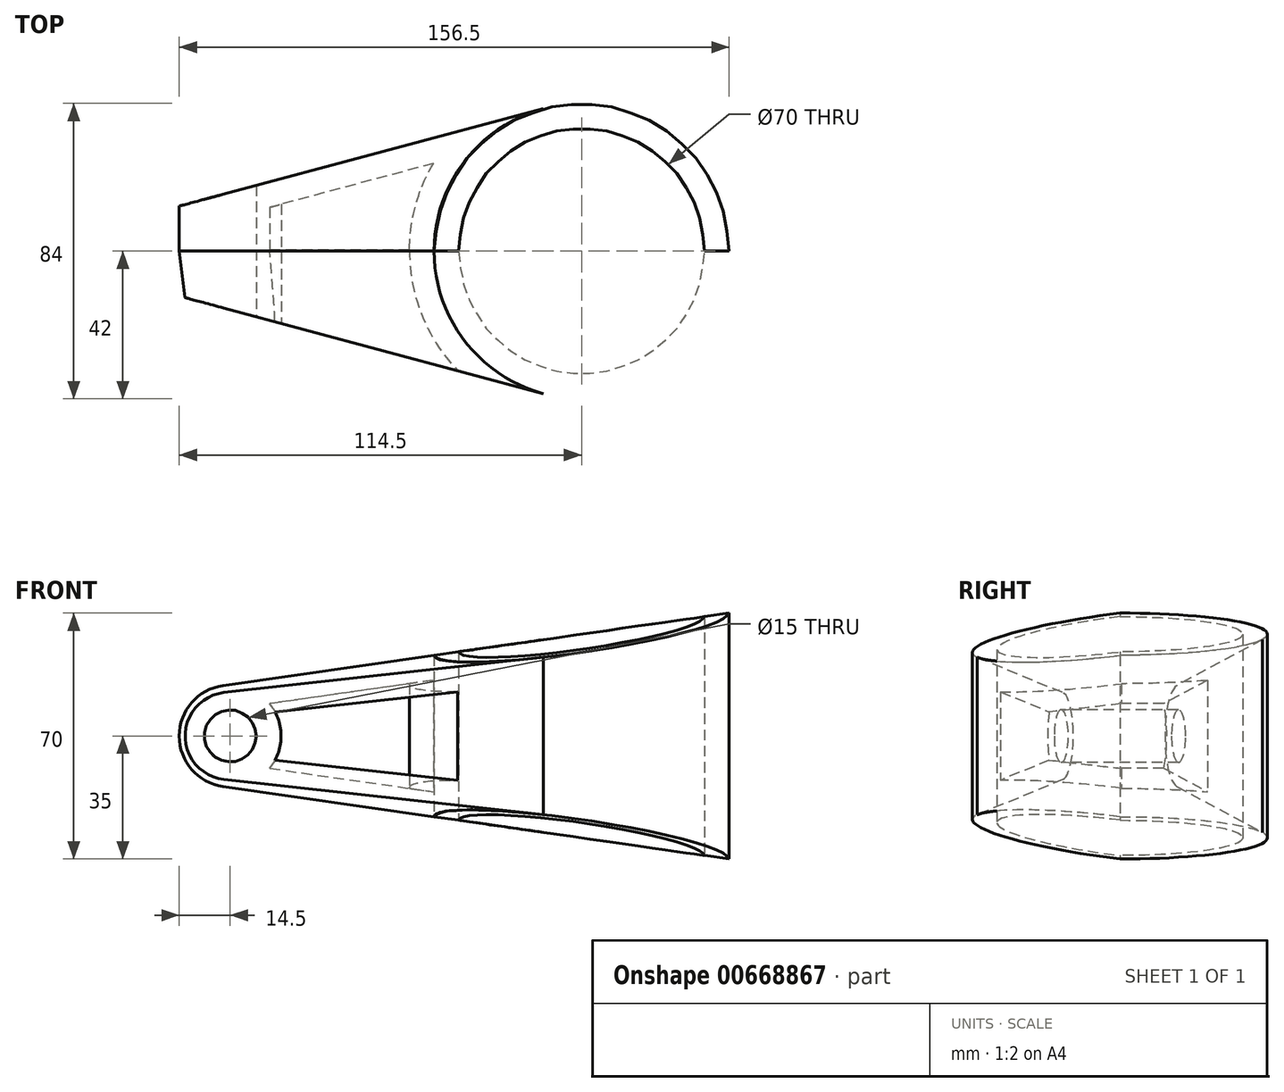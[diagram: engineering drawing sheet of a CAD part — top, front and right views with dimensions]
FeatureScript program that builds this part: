
annotation { "Feature Type Name" : "Feature", "Feature Type Description" : "" }
export const myFeature = defineFeature(function(context is Context, id is Id, definition is map)
    precondition{}
    {
        {
            var Q0;
            Q0=qCreatedBy(makeId("Top.planeOp"),FACE);
            var sketch = newSketch(context, id + "F0", { "sketchPlane" : qUnion([Q0])});
            skCircle(sketch, "E0", {"center": v(0, 0) * mm, "radius": 35 * mm});
            skCircle(sketch, "E1.0", {"center": v(0, 0) * mm, "radius": 42 * mm});
            skLineSegment(sketch, "E2", {"start": v(-100, 39.97) * mm, "end": v(-100, -35.77) * mm, "construction": true});
            skLineSegment(sketch, "E3.0", {"start": v(-114.5, 39.97) * mm, "end": v(-114.5, -35.77) * mm, "construction": true});
            skLineSegment(sketch, "E4", {"start": v(-10.87, 40.57) * mm, "end": v(-114.5, 12.8) * mm});
            skLineSegment(sketch, "E5", {"start": v(-114.5, 12.8) * mm, "end": v(-114.5, -12.8) * mm});
            skLineSegment(sketch, "E6", {"start": v(-114.5, -12.8) * mm, "end": v(-10.87, -40.57) * mm});
            skSolve(sketch);
        }
        {
            var Q0;
            Q0=makeQuery(id+"F0.imprint","IMPRINT",FACE,{"disambiguationData":[TD([[makeQuery(id+"F0.imprint","IMPRINT",EDGE,{"derivedFrom":sQuery(id+"F0.wireOp",EDGE,"E0")}),-1.0]])]});
            extrude(context, id + "F1", {"entities" : qUnion([Q0]), "endBound" : BoundingType.SYMMETRIC, "depth" : 70 * mm, "offsetDistance" : 25 * mm});
        }
        {
            var Q0;
            {var subQ0=sQuery(id+"F0.wireOp",EDGE,"E4");Q0=makeQuery(id+"F0.imprint","IMPRINT",FACE,{"disambiguationData":[TD([[makeQuery(id+"F0.imprint","IMPRINT",EDGE,{"derivedFrom":subQ0}),1.0]])]});}
            extrude(context, id + "F2", {"entities" : qUnion([Q0]), "endBound" : BoundingType.SYMMETRIC, "depth" : 70 * mm, "offsetDistance" : 25 * mm});
        }
        {
            var Q0;
            Q0=qCreatedBy(makeId("Front.planeOp"),FACE);
            var sketch = newSketch(context, id + "F3", { "sketchPlane" : qUnion([Q0])});
            skLineSegment(sketch, "E7.0", {"start": v(-42, 0) * mm, "end": v(42, 0) * mm});
            skCircle(sketch, "E8", {"center": v(-100, 0) * mm, "radius": 7.5 * mm});
            skLineSegment(sketch, "E9", {"start": v(42, 35) * mm, "end": v(-102.06, 14.35) * mm});
            skArc(sketch, "E10", {"start": v(-102.06, 14.35) * mm, "mid": v(-114.5, 0) * mm, "end": v(-102.06, -14.35) * mm});
            skLineSegment(sketch, "E11", {"start": v(-102.06, -14.35) * mm, "end": v(42, -35) * mm});
            skLineSegment(sketch, "E12", {"start": v(42, 35) * mm, "end": v(42, -35) * mm});
            skLineSegment(sketch, "E13", {"start": v(-42, -22.96) * mm, "end": v(-42, 22.96) * mm});
            skLineSegment(sketch, "E14.0", {"start": v(-42, 35) * mm, "end": v(42, 35) * mm});
            skLineSegment(sketch, "E15.0", {"start": v(-42, -35) * mm, "end": v(42, -35) * mm});
            skLineSegment(sketch, "E16.0.0", {"start": v(-10.87, 35) * mm, "end": v(-42, 35) * mm});
            skLineSegment(sketch, "E16.0.1", {"start": v(-10.87, 35) * mm, "end": v(-114.5, 35) * mm});
            skLineSegment(sketch, "E16.0.3", {"start": v(-114.5, 35) * mm, "end": v(-10.87, 35) * mm});
            skLineSegment(sketch, "E17.0.0", {"start": v(-114.5, -35) * mm, "end": v(-10.87, -35) * mm});
            skLineSegment(sketch, "E17.0.1", {"start": v(-10.87, -27.42) * mm, "end": v(-10.87, 27.42) * mm});
            skLineSegment(sketch, "E17.0.3", {"start": v(-114.5, 35) * mm, "end": v(-114.5, -35) * mm});
            skSolve(sketch);
        }
        {
            var Q0;
            {var subQ7=sQuery(id+"F3.wireOp",EDGE,"E14.0");Q0=makeQuery(id+"F3.imprint","IMPRINT",FACE,{"disambiguationData":[TD([[makeQuery(id+"F3.imprint","IMPRINT",EDGE,{"derivedFrom":subQ7}),-1.0]])]});}
            var Q1;
            {var subQ0=sQuery(id+"F3.wireOp",EDGE,"E15.0");Q1=makeQuery(id+"F3.imprint","IMPRINT",FACE,{"disambiguationData":[TD([[makeQuery(id+"F3.imprint","IMPRINT",EDGE,{"derivedFrom":subQ0}),1.0]])]});}
            var Q2;
            Q2=makeQuery(id+"F3.imprint","IMPRINT",FACE,{"disambiguationData":[TD([[makeQuery(id+"F3.imprint","IMPRINT",EDGE,{"derivedFrom":sQuery(id+"F3.wireOp",EDGE,"E8")}),1.0]])]});
            extrude(context, id + "F4", {"entities" : qUnion([Q0, Q1, Q2]), "operationType" : NewBodyOperationType.REMOVE, "endBound" : BoundingType.THROUGH_ALL, "oppositeDirection" : true, "depth" : 25 * mm, "offsetDistance" : 25 * mm, "hasSecondDirection" : true, "secondDirectionBound" : SecondDirectionBoundingType.THROUGH_ALL, "secondDirectionOppositeDirection" : false, "secondDirectionDepth" : 25 * mm});
        }
        {
            var Q0;
            Q0=qCreatedBy(makeId("Front.planeOp"),FACE);
            var sketch = newSketch(context, id + "F5", { "sketchPlane" : qUnion([Q0])});
            skLineSegment(sketch, "E18.0.0", {"start": v(-10.87, 27.42) * mm, "end": v(-102.06, 14.35) * mm, "construction": true});
            skLineSegment(sketch, "E18.0.2", {"start": v(-102.06, 14.35) * mm, "end": v(-10.87, 27.42) * mm, "construction": true});
            skLineSegment(sketch, "E18.0.3", {"start": v(-10.87, 27.42) * mm, "end": v(-42, 22.96) * mm, "construction": true});
            skLineSegment(sketch, "E19.0.0", {"start": v(42, 35) * mm, "end": v(-42, 22.96) * mm, "construction": true});
            skArc(sketch, "E20.0.0", {"start": v(-102.06, 14.35) * mm, "mid": v(-114.5, 0) * mm, "end": v(-102.06, -14.35) * mm, "construction": true});
            skArc(sketch, "E20.0.2", {"start": v(-102.06, -14.35) * mm, "mid": v(-114.5, 0) * mm, "end": v(-102.06, 14.35) * mm});
            skLineSegment(sketch, "E21.0.0", {"start": v(-102.06, -14.35) * mm, "end": v(-10.87, -27.42) * mm, "construction": true});
            skLineSegment(sketch, "E21.0.1", {"start": v(-10.87, -27.42) * mm, "end": v(-42, -22.96) * mm, "construction": true});
            skLineSegment(sketch, "E21.0.2", {"start": v(-10.87, -27.42) * mm, "end": v(-102.06, -14.35) * mm, "construction": true});
            skLineSegment(sketch, "E22.0.0", {"start": v(-42, -22.96) * mm, "end": v(42, -35) * mm, "construction": true});
            skLineSegment(sketch, "E23", {"start": v(42, 35) * mm, "end": v(-102.06, 14.35) * mm});
            skLineSegment(sketch, "E24", {"start": v(42, -35) * mm, "end": v(-102.06, -14.35) * mm});
            skSolve(sketch);
        }
        {
            var Q0;
            Q0=sQuery(id+"F5.wireOp",VERTEX,"E19.0.0.start");
            var Q1;
            Q1=sQuery(id+"F5.wireOp",EDGE,"E23");
            cPlane(context, id + "F6", {"entities" : qUnion([Q0, Q1]), "cplaneType" : CPlaneType.LINE_POINT, "offset" : 25 * mm, "width" : 150 * mm, "height" : 150 * mm});
        }
        {
            var Q0;
            Q0=qCreatedBy(id+"F6.planeOp",FACE);
            var sketch = newSketch(context, id + "F7", { "sketchPlane" : qUnion([Q0])});
            skLineSegment(sketch, "E25.0", {"start": v(-42, 28.69) * mm, "end": v(42, 28.69) * mm});
            skLineSegment(sketch, "E26", {"start": v(42, 28.69) * mm, "end": v(42, -28.69) * mm});
            skLineSegment(sketch, "E27", {"start": v(0, 28.69) * mm, "end": v(42, 23.53) * mm});
            skSolve(sketch);
        }
        {
            var Q0;
            {var subQ3=sQuery(id+"F7.wireOp",EDGE,"E27");Q0=makeQuery(id+"F7.imprint","IMPRINT",FACE,{"disambiguationData":[TD([[makeQuery(id+"F7.imprint","IMPRINT",EDGE,{"derivedFrom":subQ3}),1.0]])]});}
            var Q1;
            Q1=sQuery(id+"F5.wireOp",EDGE,"E23");
            var Q2;
            Q2=sQuery(id+"F5.wireOp",EDGE,"E20.0.2");
            var Q3;
            Q3=sQuery(id+"F5.wireOp",EDGE,"E24");
            sweep(context, id + "F8", {"operationType" : NewBodyOperationType.REMOVE, "profiles" : qUnion([Q0]), "path" : qUnion([Q1, Q2, Q3])});
        }
        {
            var Q0;
            Q0=qCreatedBy(makeId("Front.planeOp"),FACE);
            cPlane(context, id + "F9", {"entities" : qUnion([Q0]), "cplaneType" : CPlaneType.OFFSET, "offset" : 50 * mm, "width" : 150 * mm, "height" : 150 * mm});
        }
        {
            var Q0;
            Q0=makeQuery(id+"F2.opExtrude","SWEPT_FACE",FACE,{"disambiguationData":[OSD([sQuery(id+"F0.wireOp",EDGE,"E6")])]});
            shell(context, id + "F10", {"entities" : qUnion([Q0]), "thickness" : 7 * mm});
        }
    });
